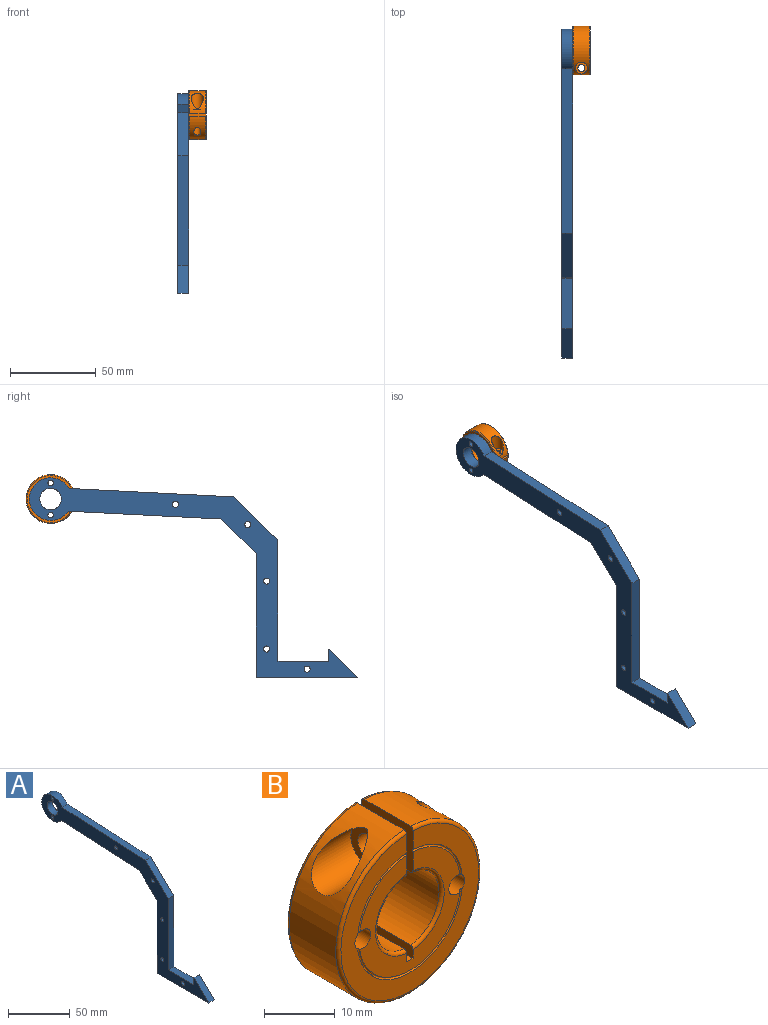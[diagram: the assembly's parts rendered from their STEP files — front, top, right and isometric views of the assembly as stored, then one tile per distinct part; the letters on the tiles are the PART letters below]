
ASSEMBLY  parts=2 mates=1
PART A: 21 faces, bbox 6.4x192x116.6 mm
  f0: cylinder r=12.44mm len=24.88mm, axis (-1,0,0), area 407.3mm2, adj f1,f10,f12,f13
  f1: plane 96.11x6.35mm, normal (0,-0.05,1), area 611.1mm2, adj f0,f2,f12,f13
  f2: plane 25.97x25.14mm, normal (0,-0.7,0.72), area 229.5mm2, adj f1,f3,f12,f13
  f3: plane 70.79x6.35mm, normal (0,-1,0), area 449.5mm2, adj f2,f4,f12,f13
  f4: plane 29.53x6.35mm, normal (0,0,1), area 187.5mm2, adj f3,f5,f12,f13
  f5: plane 7.04x6.35mm, normal (0,1,0), area 44.7mm2, adj f4,f6,f12,f13
  f6: plane 17.13x16.56mm, normal (0,-0.7,0.72), area 151.3mm2, adj f5,f7,f12,f13
  f7: plane 59.36x6.35mm, normal (0,0,-1), area 376.9mm2, adj f6,f8,f12,f13
  f8: plane 72.39x6.35mm, normal (0,1,0), area 459.7mm2, adj f7,f9,f12,f13
  f9: plane 20.82x20.16mm, normal (0,0.7,-0.72), area 184mm2, adj f8,f10,f12,f13
  f10: plane 89.12x6.35mm, normal (0,0.05,-1), area 566.7mm2, adj f0,f9,f12,f13
  f11: cylinder r=6.35mm len=12.7mm, axis (-1,0,0), area 253.4mm2, adj f12,f13
  f12: plane 191.96x116.62mm, normal (1,0,0), area 3374.2mm2, adj f0,f1,f2,f3,f4,f5,f6,f7
  f13: plane 191.96x116.62mm, normal (-1,0,0), area 3374.2mm2, adj f0,f1,f2,f3,f4,f5,f6,f7
  f14: cylinder r=1.59mm len=6.35mm, axis (1,0,0), area 63.3mm2, adj f12,f13
  f15: cylinder r=1.59mm len=6.35mm, axis (1,0,0), area 63.3mm2, adj f12,f13
  f16: cylinder r=1.78mm len=6.35mm, axis (1,0,0), area 70.9mm2, adj f12,f13
  f17: cylinder r=1.78mm len=6.35mm, axis (1,0,0), area 70.9mm2, adj f12,f13
  f18: cylinder r=1.78mm len=6.35mm, axis (1,0,0), area 70.9mm2, adj f12,f13
  f19: cylinder r=1.78mm len=6.35mm, axis (1,0,0), area 70.9mm2, adj f12,f13
  f20: cylinder r=1.78mm len=6.35mm, axis (1,0,0), area 70.9mm2, adj f12,f13
PART B: 26 faces, bbox 30.9x10.5x30.9 mm
  f0: torus R=10.32mm, axis (0,1,0), area 8.5mm2, adj f4,f5,f11,f25
  f1: torus R=10.32mm, axis (0,1,0), area 8.5mm2, adj f2,f5,f11,f24
  f2: plane 10.34x7.97mm, normal (1,0,0), area 68.2mm2, adj f1,f3,f5,f9,f11,f12,f15,f16
  f3: cylinder r=14.29mm len=28.58mm, axis (0,1,0), area 741mm2, adj f2,f4,f15,f16,f20,f21
  f4: plane 10.34x7.97mm, normal (-1,0,0), area 68.2mm2, adj f0,f3,f5,f10,f11,f12,f13,f14
  f5: plane 27.54x27.53mm, normal (0,-1,0), area 243.1mm2, adj f0,f1,f2,f4,f15,f19,f24,f25
  f6: plane 10.34x2.04mm, normal (-1,0,0), area 20.7mm2, adj f7,f10,f11,f12,f13,f14
  f7: plane 10.32x1.27mm, normal (0,0,1), area 13.1mm2, adj f6,f8,f11,f12
  f8: plane 10.34x2.04mm, normal (1,0,0), area 20.7mm2, adj f7,f9,f11,f12,f17,f18
  f9: cylinder r=6.35mm len=12.64mm, axis (0,1,0), area 173.5mm2, adj f2,f8,f17,f18
  f10: cylinder r=6.35mm len=12.64mm, axis (0,1,0), area 173.5mm2, adj f4,f6,f13,f14
  f11: plane 20.24x20.05mm, normal (0,-1,0), area 155.9mm2, adj f0,f1,f2,f4,f6,f7,f8,f13
  f12: plane 27.54x27.53mm, normal (0,1,0), area 421.2mm2, adj f2,f4,f6,f7,f8,f14,f16,f18
  f13: torus R=6.87mm, axis (0,-1,0), area 15.6mm2, adj f4,f6,f10,f11
  f14: torus R=6.87mm, axis (0,-1,0), area 15.6mm2, adj f4,f6,f10,f12
  f15: torus R=13.77mm, axis (0,-1,0), area 70.8mm2, adj f2,f3,f4,f5
  f16: torus R=13.77mm, axis (0,-1,0), area 70.8mm2, adj f2,f3,f4,f12
  f17: torus R=6.87mm, axis (0,-1,0), area 15.6mm2, adj f2,f8,f9,f11
  f18: torus R=6.87mm, axis (0,-1,0), area 15.6mm2, adj f2,f8,f9,f12
  f19: torus R=10.32mm, axis (0,1,0), area 17.8mm2, adj f5,f11,f24,f25
  f20: cylinder r=2.08mm len=11.06mm, axis (1,0,0), area 118.2mm2, adj f3,f4
  f21: cylinder r=3.49mm len=9.44mm, axis (1,0,0), area 131.4mm2, adj f3,f23
  f22: cylinder r=2.08mm len=4.17mm, axis (1,0,0), area 32.6mm2, adj f2,f23
  f23: plane 6.99x6.99mm, normal (-1,0,0), area 24.7mm2, adj f21,f22
  f24: cylinder r=1.59mm len=10.32mm, axis (0,1,0), area 102.8mm2, adj f1,f5,f11,f12,f19
  f25: cylinder r=1.59mm len=10.32mm, axis (0,1,0), area 102.8mm2, adj f0,f5,f11,f12,f19
PLACE A t=(-14.22,-7.71,11.74)mm
PLACE B rot(axis=(0.58,0.58,-0.58),120deg) t=(-2.71,36.29,-20.95)mm
MATE fastened B.f0 <-> A.f0  axis (-1,0,0) through (-7.87,36.29,-20.95)mm
